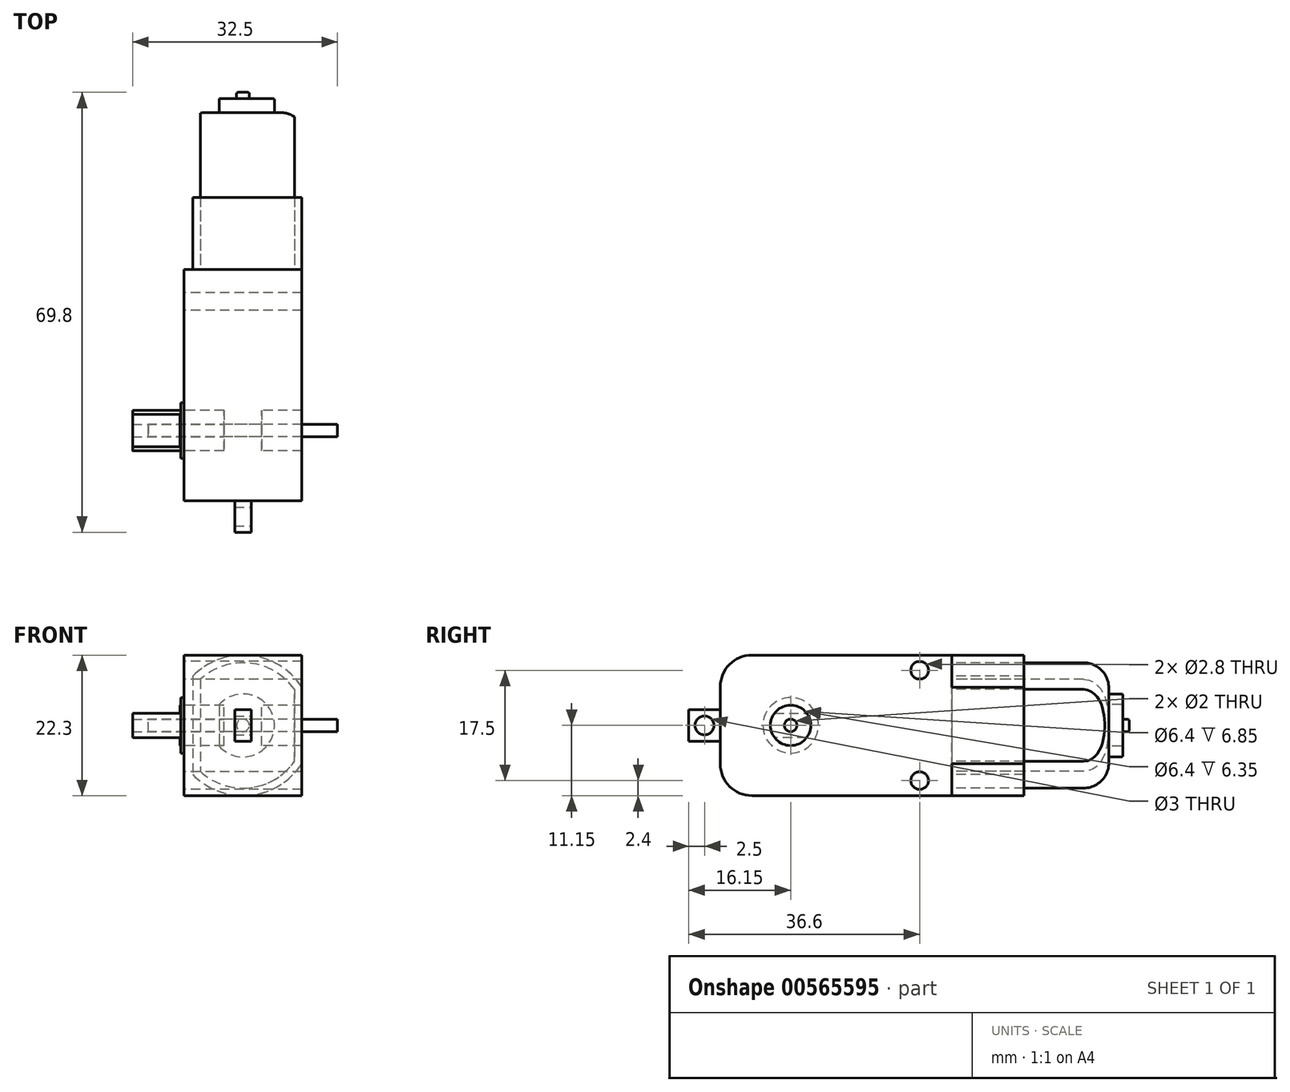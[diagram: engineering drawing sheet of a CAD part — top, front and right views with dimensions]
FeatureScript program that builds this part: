
annotation { "Feature Type Name" : "Feature", "Feature Type Description" : "" }
export const myFeature = defineFeature(function(context is Context, id is Id, definition is map)
    precondition{}
    {
        {
            var Q0;
            Q0=qCreatedBy(makeId("Right.planeOp"),FACE);
            var sketch = newSketch(context, id + "F0", { "sketchPlane" : qUnion([Q0])});
            skLineSegment(sketch, "E0.bottom", {"start": v(18.35, -11.15) * mm, "end": v(-13.35, -11.15) * mm});
            skLineSegment(sketch, "E0.top", {"start": v(18.35, 11.15) * mm, "end": v(-13.35, 11.15) * mm});
            skLineSegment(sketch, "E0.left", {"start": v(18.35, -11.15) * mm, "end": v(18.35, 11.15) * mm});
            skLineSegment(sketch, "E0.right", {"start": v(-18.35, -6.15) * mm, "end": v(-18.35, 6.15) * mm});
            skPoint(sketch, "E0.middle", {"position": v(0, 0) * mm});
            skPoint(sketch, "E1.visualSharp", {"position": v(-18.35, 11.15) * mm});
            skArc(sketch, "E1.filletArc", {"start": v(-13.35, 11.15) * mm, "mid": v(-16.89, 9.69) * mm, "end": v(-18.35, 6.15) * mm});
            skPoint(sketch, "E2.visualSharp", {"position": v(-18.35, -11.15) * mm});
            skArc(sketch, "E2.filletArc", {"start": v(-18.35, -6.15) * mm, "mid": v(-16.89, -9.69) * mm, "end": v(-13.35, -11.15) * mm});
            skLineSegment(sketch, "E3", {"start": v(-27.57, 10.15) * mm, "end": v(27, 10.15) * mm, "construction": true});
            skLineSegment(sketch, "E4", {"start": v(27, -10.15) * mm, "end": v(-33.16, -10.15) * mm, "construction": true});
            skLineSegment(sketch, "E5", {"start": v(14.65, 15.01) * mm, "end": v(14.65, -22.1) * mm, "construction": true});
            skCircle(sketch, "E6", {"center": v(13.25, 8.75) * mm, "radius": 1.4 * mm});
            skCircle(sketch, "E7.MirrorC", {"center": v(13.25, -8.75) * mm, "radius": 1.4 * mm});
            skCircle(sketch, "E8", {"center": v(-7.2, 0) * mm, "radius": 3.2 * mm});
            skCircle(sketch, "E9", {"center": v(-7.2, 0) * mm, "radius": 1 * mm});
            skSolve(sketch);
        }
        {
            var Q0;
            Q0=makeQuery(id+"F0.imprint","IMPRINT",FACE,{"disambiguationData":[TD([[makeQuery(id+"F0.imprint","IMPRINT",EDGE,{"derivedFrom":sQuery(id+"F0.wireOp",EDGE,"E0.bottom")}),-1.0]])]});
            extrude(context, id + "F1", {"entities" : qUnion([Q0]), "endBound" : BoundingType.SYMMETRIC, "depth" : (18.7) * mm});
        }
        {
            var Q0;
            Q0=makeQuery(id+"F1.opExtrude","SWEPT_FACE",FACE,{"disambiguationData":[OSD([sQuery(id+"F0.wireOp",EDGE,"E0.right")])]});
            var sketch = newSketch(context, id + "F2", { "sketchPlane" : qUnion([Q0])});
            skLineSegment(sketch, "E10.bottom", {"start": v(1.3, -2.5) * mm, "end": v(-1.3, -2.5) * mm});
            skLineSegment(sketch, "E10.top", {"start": v(1.3, 2.5) * mm, "end": v(-1.3, 2.5) * mm});
            skLineSegment(sketch, "E10.left", {"start": v(1.3, -2.5) * mm, "end": v(1.3, 2.5) * mm});
            skLineSegment(sketch, "E10.right", {"start": v(-1.3, -2.5) * mm, "end": v(-1.3, 2.5) * mm});
            skPoint(sketch, "E10.middle", {"position": v(0, 0) * mm});
            skSolve(sketch);
        }
        {
            var Q0;
            Q0=makeQuery(id+"F2.imprint","IMPRINT",FACE,{"disambiguationData":[TD([[makeQuery(id+"F2.imprint","IMPRINT",EDGE,{"derivedFrom":sQuery(id+"F2.wireOp",EDGE,"E10.bottom")}),-1.0]])]});
            extrude(context, id + "F3", {"entities" : qUnion([Q0]), "operationType" : NewBodyOperationType.ADD, "depth" : 5 * mm});
        }
        {
            var Q0;
            Q0=makeQuery(id+"F3.opExtrude","SWEPT_FACE",FACE,{"disambiguationData":[OSD([sQuery(id+"F2.wireOp",EDGE,"E10.left")])]});
            var sketch = newSketch(context, id + "F4", { "sketchPlane" : qUnion([Q0])});
            skLineSegment(sketch, "E11", {"start": v(-23.35, 0) * mm, "end": v(-18.35, 0) * mm, "construction": true});
            skCircle(sketch, "E12", {"center": v(-20.85, 0) * mm, "radius": 1.5 * mm});
            skSolve(sketch);
        }
        {
            var Q0;
            Q0=makeQuery(id+"F4.imprint","IMPRINT",FACE,{"disambiguationData":[TD([[makeQuery(id+"F4.imprint","IMPRINT",EDGE,{"derivedFrom":sQuery(id+"F4.wireOp",EDGE,"E12")}),1.0]])]});
            extrude(context, id + "F5", {"entities" : qUnion([Q0]), "operationType" : NewBodyOperationType.REMOVE, "endBound" : BoundingType.THROUGH_ALL, "oppositeDirection" : true, "depth" : 25 * mm});
        }
        {
            var Q0;
            Q0=makeQuery(id+"F1.opExtrude","SWEPT_FACE",FACE,{"disambiguationData":[OSD([sQuery(id+"F0.wireOp",EDGE,"E0.left")])]});
            var sketch = newSketch(context, id + "F6", { "sketchPlane" : qUnion([Q0])});
            skArc(sketch, "E13", {"start": v(7.95, 7.82) * mm, "mid": v(-1.12, 11.1) * mm, "end": v(-9.35, 6.07) * mm});
            skLineSegment(sketch, "E14", {"start": v(7.95, 13.91) * mm, "end": v(7.95, -13.85) * mm, "construction": true});
            skLineSegment(sketch, "E15", {"start": v(-9.35, 11.15) * mm, "end": v(-9.35, -11.15) * mm, "construction": true});
            skArc(sketch, "E16.trimOffspring", {"start": v(-9.35, -6.07) * mm, "mid": v(-1.12, -11.1) * mm, "end": v(7.95, -7.82) * mm});
            skLineSegment(sketch, "E17", {"start": v(-9.35, 6.07) * mm, "end": v(-9.35, -6.07) * mm});
            skLineSegment(sketch, "E18", {"start": v(7.95, 7.82) * mm, "end": v(7.95, -7.82) * mm});
            skArc(sketch, "E19.0", {"start": v(-8.15, -5.7) * mm, "mid": v(-1.06, -9.9) * mm, "end": v(6.75, -7.31) * mm});
            skLineSegment(sketch, "E19.1", {"start": v(-8.15, 5.7) * mm, "end": v(-8.15, -5.7) * mm});
            skArc(sketch, "E19.2", {"start": v(6.75, 7.31) * mm, "mid": v(-1.06, 9.9) * mm, "end": v(-8.15, 5.7) * mm});
            skLineSegment(sketch, "E19.3", {"start": v(6.75, 7.31) * mm, "end": v(6.75, -7.31) * mm});
            skSolve(sketch);
        }
        {
            var Q0;
            {var subQ4=sQuery(id+"F6.wireOp",EDGE,"E17");Q0=makeQuery(id+"F6.imprint","IMPRINT",FACE,{"disambiguationData":[TD([[makeQuery(id+"F6.imprint","IMPRINT",EDGE,{"derivedFrom":subQ4}),-1.0]])]});}
            extrude(context, id + "F7", {"entities" : qUnion([Q0]), "operationType" : NewBodyOperationType.ADD, "depth" : 11.4 * mm});
        }
        {
            var Q0;
            Q0=makeQuery(id+"F7.boolean.opBoolean","SPLIT",FACE,{"disambiguationData":[TD([makeQuery(id+"F7.opExtrude","SWEPT_FACE",FACE,{"disambiguationData":[OSD([sQuery(id+"F6.wireOp",EDGE,"E19.0")])]}),makeQuery(id+"F7.opExtrude","SWEPT_FACE",FACE,{"disambiguationData":[OSD([sQuery(id+"F6.wireOp",EDGE,"E19.1")])]}),makeQuery(id+"F7.opExtrude","SWEPT_FACE",FACE,{"disambiguationData":[OSD([sQuery(id+"F6.wireOp",EDGE,"E19.2")])]}),makeQuery(id+"F7.opExtrude","SWEPT_FACE",FACE,{"disambiguationData":[OSD([sQuery(id+"F6.wireOp",EDGE,"E19.3")])]})])],"derivedFrom":makeQuery(id+"F1.opExtrude","SWEPT_FACE",FACE,{"disambiguationData":[OSD([sQuery(id+"F0.wireOp",EDGE,"E0.left")])]})});
            extrude(context, id + "F8", {"entities" : qUnion([Q0]), "depth" : (11.4 + 13.5) * mm});
        }
        {
            var Q0;
            Q0=makeQuery(id+"F8.opExtrude","CAP_EDGE",EDGE,{"disambiguationData":[OSD([sQuery(id+"F6.wireOp",EDGE,"E19.0")])],"isStart":false});
            fillet(context, id + "F9", {"entities" : qUnion([Q0]), "radius" : 4 * mm, "tangentPropagation" : true, "allowEdgeOverflow" : false});
        }
        {
            var Q0;
            Q0=makeQuery(id+"F8.opExtrude","CAP_FACE",FACE,{"disambiguationData":[OSD([sQuery(id+"F0.wireOp",EDGE,"E0.left")])],"isStart":false});
            var sketch = newSketch(context, id + "F10", { "sketchPlane" : qUnion([Q0])});
            skLineSegment(sketch, "E20", {"start": v(3.75, -5.9) * mm, "end": v(3.75, 7.54) * mm, "construction": true});
            skArc(sketch, "E21", {"start": v(3.75, 3.3) * mm, "mid": v(-5, 0) * mm, "end": v(3.75, -3.3) * mm});
            skLineSegment(sketch, "E22", {"start": v(3.75, 3.3) * mm, "end": v(3.75, -3.3) * mm});
            skCircle(sketch, "E23", {"center": v(0, 0) * mm, "radius": 1 * mm});
            skSolve(sketch);
        }
        {
            var Q0;
            Q0=makeQuery(id+"F0.imprint","IMPRINT",FACE,{"disambiguationData":[TD([[makeQuery(id+"F0.imprint","IMPRINT",EDGE,{"derivedFrom":sQuery(id+"F0.wireOp",EDGE,"E8")}),1.0]])]});
            extrude(context, id + "F11", {"entities" : qUnion([Q0]), "operationType" : NewBodyOperationType.ADD, "endBound" : BoundingType.SYMMETRIC, "depth" : 6 * mm});
        }
        {
            var Q0;
            Q0=makeQuery(id+"F0.imprint","IMPRINT",FACE,{"disambiguationData":[TD([[makeQuery(id+"F0.imprint","IMPRINT",EDGE,{"derivedFrom":sQuery(id+"F0.wireOp",EDGE,"E9")}),1.0]])]});
            extrude(context, id + "F12", {"entities" : qUnion([Q0]), "endBound" : BoundingType.SYMMETRIC, "depth" : 30 * mm});
        }
        {
            var Q0;
            Q0=makeQuery(id+"F1.opExtrude","CAP_FACE",FACE,{"disambiguationData":[OSD([sQuery(id+"F0.wireOp",EDGE,"E0.bottom"),sQuery(id+"F0.wireOp",EDGE,"E0.top"),sQuery(id+"F0.wireOp",EDGE,"E0.left"),sQuery(id+"F0.wireOp",EDGE,"E0.right"),sQuery(id+"F0.wireOp",EDGE,"E1.filletArc"),sQuery(id+"F0.wireOp",EDGE,"E2.filletArc"),sQuery(id+"F0.wireOp",EDGE,"E6"),sQuery(id+"F0.wireOp",EDGE,"E7.MirrorC"),sQuery(id+"F0.wireOp",EDGE,"E8")])],"isStart":true});
            var sketch = newSketch(context, id + "F13", { "sketchPlane" : qUnion([Q0])});
            skCircle(sketch, "E24", {"center": v(7.2, 0) * mm, "radius": 3.2 * mm});
            skCircle(sketch, "E25.0", {"center": v(7.2, 0) * mm, "radius": 4.4 * mm});
            skSolve(sketch);
        }
        {
            var Q0;
            Q0=makeQuery(id+"F13.imprint","IMPRINT",FACE,{"disambiguationData":[TD([[makeQuery(id+"F13.imprint","IMPRINT",EDGE,{"derivedFrom":sQuery(id+"F13.wireOp",EDGE,"E24")}),1.0]])]});
            extrude(context, id + "F14", {"entities" : qUnion([Q0]), "operationType" : NewBodyOperationType.ADD, "depth" : .5 * mm});
        }
        {
            var Q0;
            Q0=makeQuery(id+"F11.opExtrude","CAP_FACE",FACE,{"disambiguationData":[OSD([sQuery(id+"F0.wireOp",EDGE,"E8"),sQuery(id+"F0.wireOp",EDGE,"E9")])],"isStart":true});
            var sketch = newSketch(context, id + "F15", { "sketchPlane" : qUnion([Q0])});
            skCircle(sketch, "E26", {"center": v(7.2, 0) * mm, "radius": 1 * mm});
            skCircle(sketch, "E27", {"center": v(7.2, 0) * mm, "radius": 3.2 * mm});
            skSolve(sketch);
        }
        {
            var Q0;
            Q0=makeQuery(id+"F15.imprint","IMPRINT",FACE,{"disambiguationData":[TD([[makeQuery(id+"F15.imprint","IMPRINT",EDGE,{"derivedFrom":sQuery(id+"F15.wireOp",EDGE,"E26")}),1.0]])]});
            extrude(context, id + "F16", {"entities" : qUnion([Q0]), "depth" : 14.5 * mm});
        }
        {
            var Q0;
            Q0=makeQuery(id+"F16.opExtrude","CAP_FACE",FACE,{"disambiguationData":[OSD([sQuery(id+"F15.wireOp",EDGE,"E26"),sQuery(id+"F15.wireOp",EDGE,"E27")])],"isStart":false});
            var sketch = newSketch(context, id + "F17", { "sketchPlane" : qUnion([Q0])});
            skLineSegment(sketch, "E28", {"start": v(13.52, -1.92) * mm, "end": v(0.5, -1.92) * mm, "construction": true});
            skLineSegment(sketch, "E29", {"start": v(0.5, -1.92) * mm, "end": v(0.83, 1.03) * mm, "construction": true});
            skLineSegment(sketch, "E30.MirrorCS", {"start": v(13.52, 1.92) * mm, "end": v(0.5, 1.92) * mm, "construction": true});
            skLineSegment(sketch, "E31", {"start": v(9.76, 1.92) * mm, "end": v(4.64, 1.92) * mm});
            skLineSegment(sketch, "E32", {"start": v(4.64, -1.92) * mm, "end": v(9.76, -1.92) * mm});
            skSolve(sketch);
        }
        {
            var Q0;
            {var subQ0=sQuery(id+"F17.wireOp",EDGE,"E31");Q0=makeQuery(id+"F17.imprint","IMPRINT",FACE,{"disambiguationData":[TD([[makeQuery(id+"F17.imprint","IMPRINT",EDGE,{"derivedFrom":subQ0}),-1.0]])]});}
            var Q1;
            {var subQ0=sQuery(id+"F17.wireOp",EDGE,"E32");Q1=makeQuery(id+"F17.imprint","IMPRINT",FACE,{"disambiguationData":[TD([[makeQuery(id+"F17.imprint","IMPRINT",EDGE,{"derivedFrom":subQ0}),-1.0]])]});}
            extrude(context, id + "F18", {"entities" : qUnion([Q0, Q1]), "operationType" : NewBodyOperationType.REMOVE, "oppositeDirection" : true, "depth" : 7.5 * mm, "offsetDistance" : 25 * mm});
        }
        {
            var Q0;
            Q0=makeQuery(id+"F10.imprint","IMPRINT",FACE,{"disambiguationData":[TD([[makeQuery(id+"F10.imprint","IMPRINT",EDGE,{"derivedFrom":sQuery(id+"F10.wireOp",EDGE,"E21")}),1.0]])]});
            extrude(context, id + "F19", {"entities" : qUnion([Q0]), "operationType" : NewBodyOperationType.ADD, "depth" : 2.2 * mm});
        }
        {
            var Q0;
            Q0=makeQuery(id+"F10.imprint","IMPRINT",FACE,{"disambiguationData":[TD([[makeQuery(id+"F10.imprint","IMPRINT",EDGE,{"derivedFrom":sQuery(id+"F10.wireOp",EDGE,"E23")}),1.0]])]});
            extrude(context, id + "F20", {"entities" : qUnion([Q0]), "operationType" : NewBodyOperationType.ADD, "depth" : 3.2 * mm});
        }
        {
            var Q0;
            Q0=makeQuery(id+"F19.opExtrude","CAP_EDGE",EDGE,{"disambiguationData":[OSD([sQuery(id+"F10.wireOp",EDGE,"E21")])],"isStart":false});
            var Q1;
            Q1=makeQuery(id+"F20.opExtrude","CAP_EDGE",EDGE,{"disambiguationData":[OSD([sQuery(id+"F10.wireOp",EDGE,"E23")])],"isStart":false});
            fillet(context, id + "F21", {"entities" : qUnion([Q0, Q1]), "radius" : .2 * mm, "tangentPropagation" : true, "allowEdgeOverflow" : false});
        }
    });
